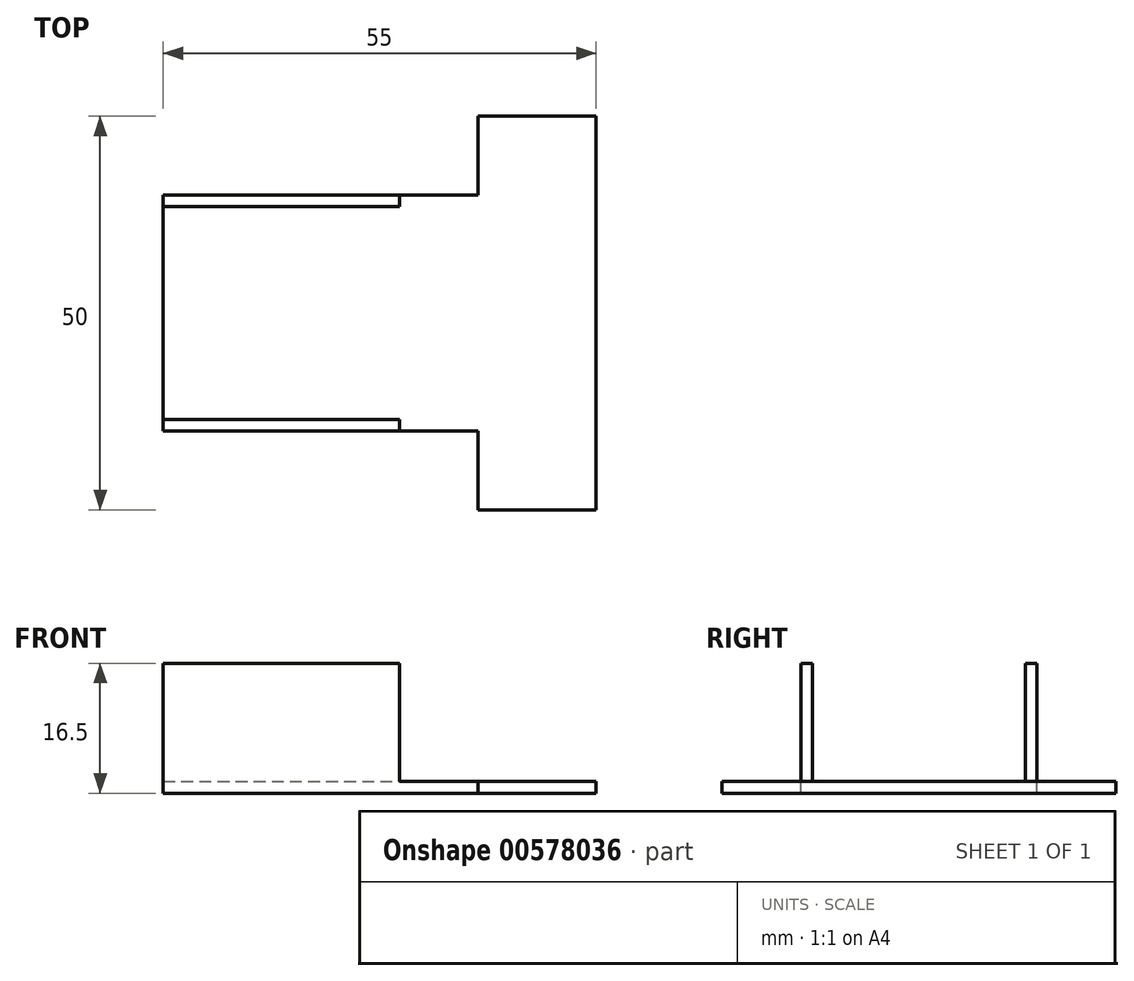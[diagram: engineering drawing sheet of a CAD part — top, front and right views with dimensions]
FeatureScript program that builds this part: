
annotation { "Feature Type Name" : "Feature", "Feature Type Description" : "" }
export const myFeature = defineFeature(function(context is Context, id is Id, definition is map)
    precondition{}
    {
        {
            var Q0;
            Q0=qCreatedBy(makeId("Top.planeOp"),FACE);
            var sketch = newSketch(context, id + "F0", { "sketchPlane" : qUnion([Q0])});
            skLineSegment(sketch, "E0.bottom", {"start": v(-15, 15) * mm, "end": v(15, 15) * mm});
            skLineSegment(sketch, "E0.top", {"start": v(-15, -15) * mm, "end": v(15, -15) * mm});
            skLineSegment(sketch, "E0.left", {"start": v(-15, 15) * mm, "end": v(-15, -15) * mm});
            skLineSegment(sketch, "E0.right", {"start": v(15, 15) * mm, "end": v(15, -15) * mm});
            skSolve(sketch);
        }
        {
            var Q0;
            Q0 = qSketchRegion(id + "F0", true);
            extrude(context, id + "F1", {"entities" : qUnion([Q0]), "depth" : 1.5 * mm, "offsetDistance" : 25 * mm});
        }
        {
            var Q0;
            Q0=makeQuery(id+"F1.opExtrude","CAP_FACE",FACE,{"disambiguationData":[OSD([sQuery(id+"F0.wireOp",EDGE,"E0.bottom"),sQuery(id+"F0.wireOp",EDGE,"E0.top"),sQuery(id+"F0.wireOp",EDGE,"E0.left"),sQuery(id+"F0.wireOp",EDGE,"E0.right")])],"isStart":false});
            var sketch = newSketch(context, id + "F2", { "sketchPlane" : qUnion([Q0])});
            skLineSegment(sketch, "E1", {"start": v(15, 15) * mm, "end": v(25, 15) * mm});
            skLineSegment(sketch, "E2", {"start": v(25, 15) * mm, "end": v(25, 25) * mm});
            skLineSegment(sketch, "E3", {"start": v(25, 25) * mm, "end": v(40, 25) * mm});
            skLineSegment(sketch, "E4", {"start": v(15, -15) * mm, "end": v(25, -15) * mm});
            skLineSegment(sketch, "E5", {"start": v(25, -15) * mm, "end": v(25, -25) * mm});
            skLineSegment(sketch, "E6", {"start": v(25, -25) * mm, "end": v(40, -25) * mm});
            skLineSegment(sketch, "E7", {"start": v(40, -25) * mm, "end": v(40, 25) * mm});
            skSolve(sketch);
        }
        {
            var Q0;
            Q0=makeQuery(id+"F2.imprint","IMPRINT",FACE,{"disambiguationData":[TD([[makeQuery(id+"F2.imprint","IMPRINT",EDGE,{"derivedFrom":sQuery(id+"F2.wireOp",EDGE,"E1")}),-1.0]])]});
            extrude(context, id + "F3", {"entities" : qUnion([Q0]), "oppositeDirection" : true, "depth" : 1.5 * mm, "offsetDistance" : 25 * mm});
        }
        {
            var Q0;
            Q0=makeQuery(id+"F1.opExtrude","CAP_FACE",FACE,{"disambiguationData":[OSD([sQuery(id+"F0.wireOp",EDGE,"E0.bottom"),sQuery(id+"F0.wireOp",EDGE,"E0.top"),sQuery(id+"F0.wireOp",EDGE,"E0.left"),sQuery(id+"F0.wireOp",EDGE,"E0.right")])],"isStart":false});
            var sketch = newSketch(context, id + "F4", { "sketchPlane" : qUnion([Q0])});
            skLineSegment(sketch, "E8.bottom", {"start": v(-15, 15) * mm, "end": v(15, 15) * mm});
            skLineSegment(sketch, "E8.top", {"start": v(-15, 13.5) * mm, "end": v(15, 13.5) * mm});
            skLineSegment(sketch, "E8.left", {"start": v(-15, 15) * mm, "end": v(-15, 13.5) * mm});
            skLineSegment(sketch, "E8.right", {"start": v(15, 15) * mm, "end": v(15, 13.5) * mm});
            skSolve(sketch);
        }
        {
            var Q0;
            Q0=makeQuery(id+"F4.imprint","IMPRINT",FACE,{"disambiguationData":[TD([[makeQuery(id+"F4.imprint","IMPRINT",EDGE,{"derivedFrom":sQuery(id+"F4.wireOp",EDGE,"E8.bottom")}),-1.0]])]});
            extrude(context, id + "F5", {"entities" : qUnion([Q0]), "operationType" : NewBodyOperationType.ADD, "depth" : 15 * mm, "offsetDistance" : 25 * mm});
        }
        {
            var Q0;
            Q0=makeQuery(id+"F1.opExtrude","CAP_FACE",FACE,{"disambiguationData":[OSD([sQuery(id+"F0.wireOp",EDGE,"E0.bottom"),sQuery(id+"F0.wireOp",EDGE,"E0.top"),sQuery(id+"F0.wireOp",EDGE,"E0.left"),sQuery(id+"F0.wireOp",EDGE,"E0.right")])],"isStart":false});
            var sketch = newSketch(context, id + "F6", { "sketchPlane" : qUnion([Q0])});
            skLineSegment(sketch, "E9.bottom", {"start": v(-15, -15) * mm, "end": v(15, -15) * mm});
            skLineSegment(sketch, "E9.top", {"start": v(-15, -13.5) * mm, "end": v(15, -13.5) * mm});
            skLineSegment(sketch, "E9.left", {"start": v(-15, -15) * mm, "end": v(-15, -13.5) * mm});
            skLineSegment(sketch, "E9.right", {"start": v(15, -15) * mm, "end": v(15, -13.5) * mm});
            skSolve(sketch);
        }
        {
            var Q0;
            Q0=makeQuery(id+"F6.imprint","IMPRINT",FACE,{"disambiguationData":[TD([[makeQuery(id+"F6.imprint","IMPRINT",EDGE,{"derivedFrom":sQuery(id+"F6.wireOp",EDGE,"E9.bottom")}),1.0]])]});
            extrude(context, id + "F7", {"entities" : qUnion([Q0]), "operationType" : NewBodyOperationType.ADD, "depth" : 15 * mm, "offsetDistance" : 25 * mm});
        }
    });
